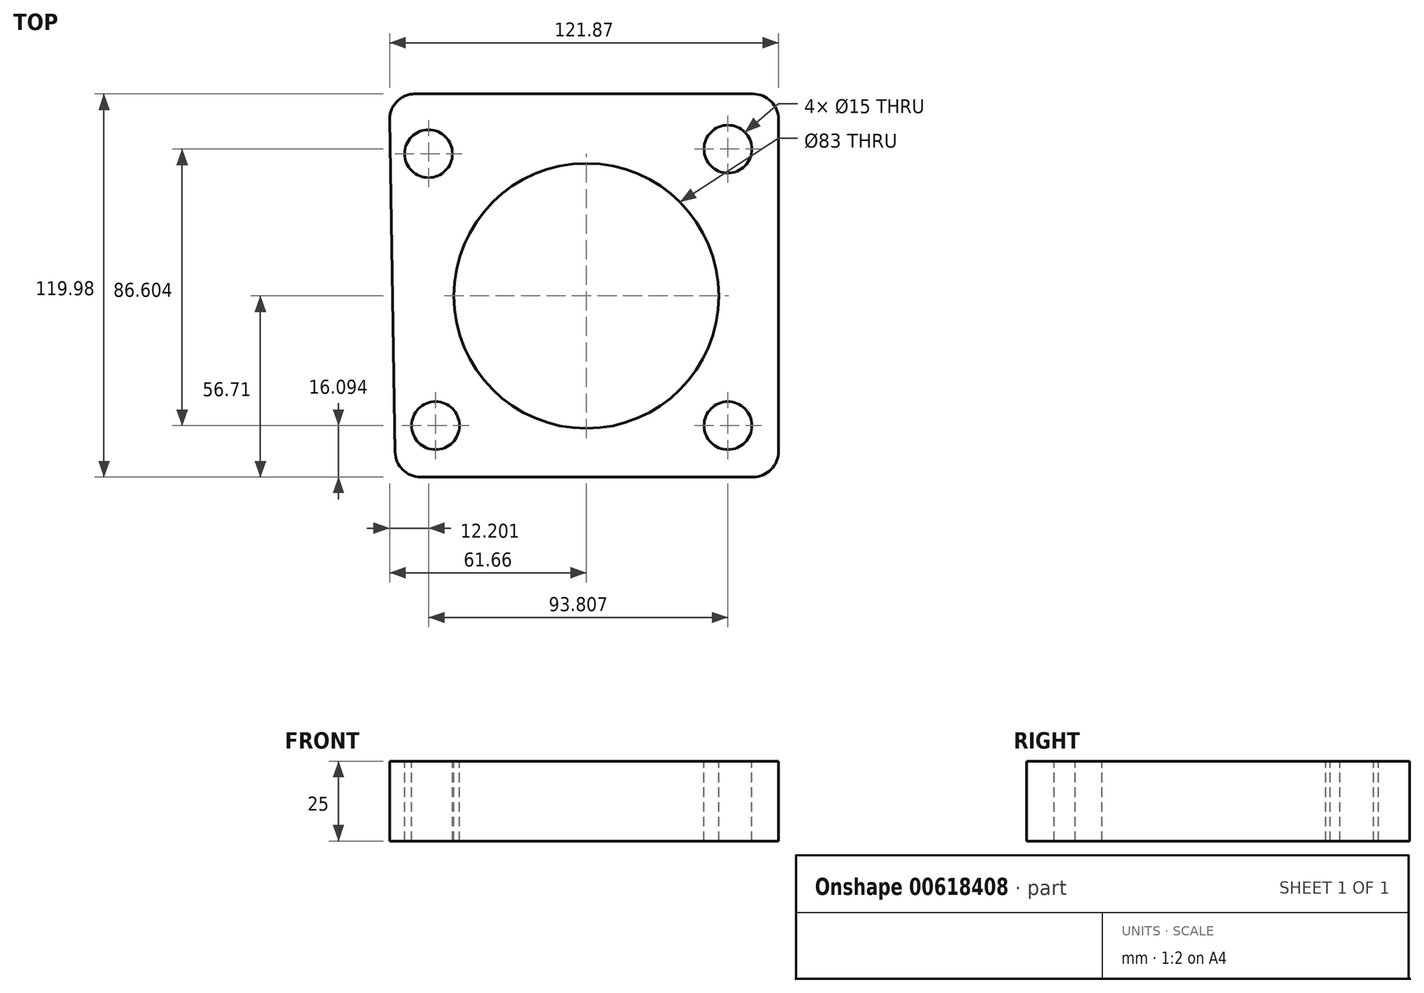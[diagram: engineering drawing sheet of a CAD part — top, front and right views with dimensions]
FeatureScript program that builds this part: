
annotation { "Feature Type Name" : "Feature", "Feature Type Description" : "" }
export const myFeature = defineFeature(function(context is Context, id is Id, definition is map)
    precondition{}
    {
        {
            var Q0;
            Q0=qCreatedBy(makeId("Top.planeOp"),FACE);
            var sketch = newSketch(context, id + "F0", { "sketchPlane" : qUnion([Q0])});
            skLineSegment(sketch, "E0", {"start": v(-51.93, -56.7) * mm, "end": v(52.2, -56.7) * mm});
            skLineSegment(sketch, "E1", {"start": v(60.2, -48.7) * mm, "end": v(60.2, 55.27) * mm});
            skLineSegment(sketch, "E2", {"start": v(52.2, 63.27) * mm, "end": v(-53.66, 63.27) * mm});
            skLineSegment(sketch, "E3", {"start": v(-61.65, 55.14) * mm, "end": v(-59.93, -48.84) * mm});
            skCircle(sketch, "E4", {"center": v(0, 0) * mm, "radius": 41.5 * mm});
            skCircle(sketch, "E5", {"center": v(-49.46, 44.54) * mm, "radius": 7.5 * mm});
            skCircle(sketch, "E6", {"center": v(-47.25, -40.62) * mm, "radius": 7.5 * mm});
            skCircle(sketch, "E7", {"center": v(44.35, -40.62) * mm, "radius": 7.5 * mm});
            skCircle(sketch, "E8", {"center": v(44.35, 45.99) * mm, "radius": 7.5 * mm});
            skPoint(sketch, "E9.visualSharp", {"position": v(-61.8, 63.27) * mm});
            skArc(sketch, "E9.filletArc", {"start": v(-53.66, 63.27) * mm, "mid": v(-59.36, 60.88) * mm, "end": v(-61.65, 55.14) * mm});
            skPoint(sketch, "E10.visualSharp", {"position": v(-59.8, -56.7) * mm});
            skArc(sketch, "E10.filletArc", {"start": v(-59.93, -48.84) * mm, "mid": v(-57.54, -54.41) * mm, "end": v(-51.93, -56.7) * mm});
            skPoint(sketch, "E11.visualSharp", {"position": v(60.2, -56.7) * mm});
            skArc(sketch, "E11.filletArc", {"start": v(52.2, -56.7) * mm, "mid": v(57.86, -54.37) * mm, "end": v(60.2, -48.7) * mm});
            skPoint(sketch, "E12.visualSharp", {"position": v(60.2, 63.27) * mm});
            skArc(sketch, "E12.filletArc", {"start": v(60.2, 55.27) * mm, "mid": v(57.86, 60.93) * mm, "end": v(52.2, 63.27) * mm});
            skSolve(sketch);
        }
        {
            var Q0;
            Q0=makeQuery(id+"F0.imprint","IMPRINT",FACE,{"disambiguationData":[TD([[makeQuery(id+"F0.imprint","IMPRINT",EDGE,{"derivedFrom":sQuery(id+"F0.wireOp",EDGE,"E0")}),1.0]])]});
            extrude(context, id + "F1", {"entities" : qUnion([Q0]), "oppositeDirection" : true, "depth" : 25 * mm, "offsetDistance" : 25 * mm});
        }
    });
